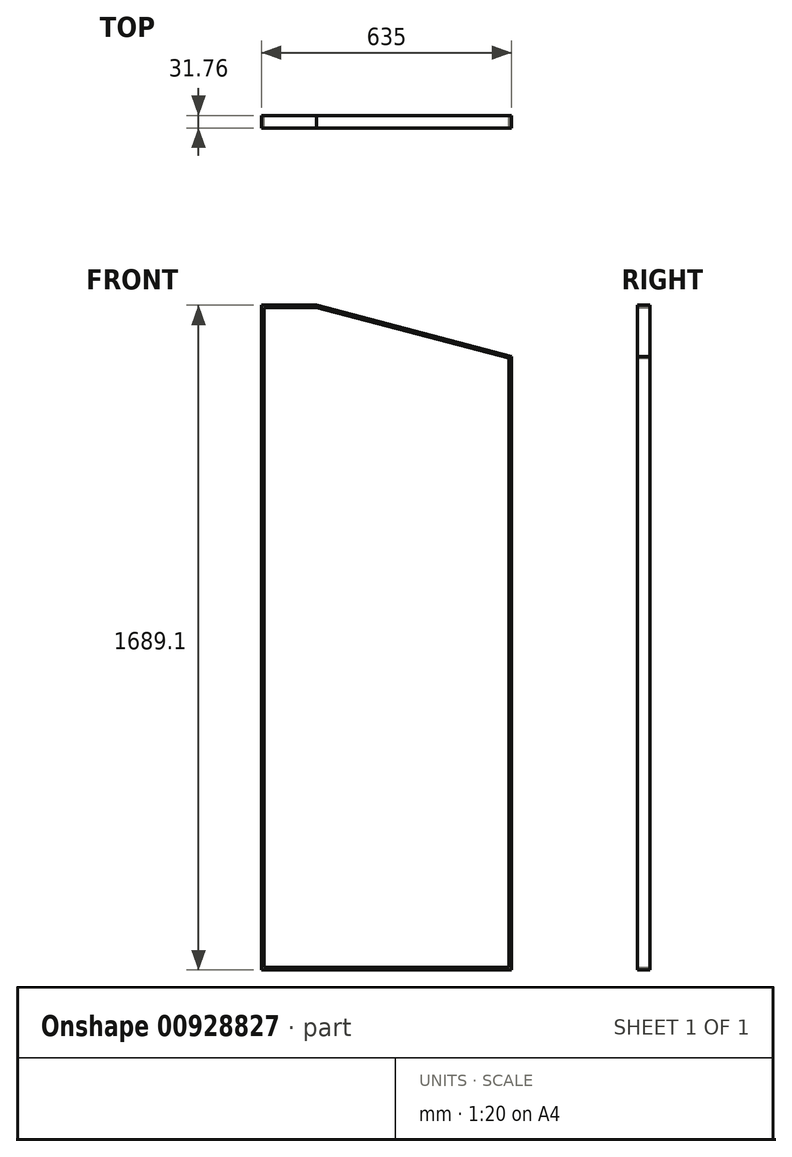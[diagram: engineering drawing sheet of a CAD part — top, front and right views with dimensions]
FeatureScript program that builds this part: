
annotation { "Feature Type Name" : "Feature", "Feature Type Description" : "" }
export const myFeature = defineFeature(function(context is Context, id is Id, definition is map)
    precondition{}
    {
        {
            var Q0;
            Q0=qCreatedBy(makeId("Front.planeOp"),FACE);
            var sketch = newSketch(context, id + "F0", { "sketchPlane" : qUnion([Q0])});
            skLineSegment(sketch, "E0.bottom", {"start": v(0, 0) * mm, "end": v(635, 0) * mm});
            skLineSegment(sketch, "E0.left", {"start": v(0, 0) * mm, "end": v(0, 1689.1) * mm});
            skLineSegment(sketch, "E0.right", {"start": v(635, 0) * mm, "end": v(635, 1558.93) * mm});
            skLineSegment(sketch, "E1", {"start": v(0, 1689.1) * mm, "end": v(139.7, 1689.1) * mm});
            skLineSegment(sketch, "E2", {"start": v(139.7, 1689.1) * mm, "end": v(635, 1558.92) * mm});
            skSolve(sketch);
        }
        {
            var Q0;
            Q0=makeQuery(id+"F0.imprint","IMPRINT",FACE,{"disambiguationData":[TD([[makeQuery(id+"F0.imprint","IMPRINT",EDGE,{"derivedFrom":sQuery(id+"F0.wireOp",EDGE,"E0.bottom")}),1.0]])]});
            extrude(context, id + "F1", {"entities" : qUnion([Q0]), "oppositeDirection" : true, "depth" : 1 / 101.6 * mm, "offsetDistance" : 25.4 * mm});
        }
        {
            var Q0;
            Q0=qCreatedBy(makeId("Front.planeOp"),FACE);
            var sketch = newSketch(context, id + "F2", { "sketchPlane" : qUnion([Q0])});
            skLineSegment(sketch, "E3.0.0", {"start": v(635, 1558.92) * mm, "end": v(139.7, 1689.1) * mm});
            skLineSegment(sketch, "E3.0.1", {"start": v(139.7, 1689.1) * mm, "end": v(0, 1689.1) * mm});
            skLineSegment(sketch, "E3.0.3", {"start": v(0, 0) * mm, "end": v(635, 0) * mm});
            skLineSegment(sketch, "E3.0.4", {"start": v(635, 0) * mm, "end": v(635, 1558.93) * mm});
            skLineSegment(sketch, "E4.bottom", {"start": v(0, 1689.1) * mm, "end": v(139.7, 1689.1) * mm});
            skLineSegment(sketch, "E4.top", {"start": v(6.35, 1682.75) * mm, "end": v(139.7, 1682.75) * mm});
            skLineSegment(sketch, "E5", {"start": v(139.7, 1689.1) * mm, "end": v(635, 1558.92) * mm});
            skLineSegment(sketch, "E6", {"start": v(139.7, 1682.75) * mm, "end": v(628.65, 1554.24) * mm});
            skLineSegment(sketch, "E7", {"start": v(0, 1689.1) * mm, "end": v(0, 0) * mm});
            skLineSegment(sketch, "E8", {"start": v(6.35, 1682.75) * mm, "end": v(6.35, 6.35) * mm});
            skPoint(sketch, "E9.orphan", {"position": v(0, 2.01) * mm});
            skLineSegment(sketch, "E10", {"start": v(6.35, 6.35) * mm, "end": v(628.65, 6.35) * mm});
            skLineSegment(sketch, "E11", {"start": v(628.65, 1554.24) * mm, "end": v(628.65, 6.35) * mm});
            skSolve(sketch);
        }
        {
            var Q0;
            Q0=makeQuery(id+"F2.imprint","IMPRINT",FACE,{"disambiguationData":[TD([[makeQuery(id+"F2.imprint","IMPRINT",EDGE,{"derivedFrom":sQuery(id+"F2.wireOp",EDGE,"E3.0.3")}),1.0]])]});
            extrude(context, id + "F3", {"entities" : qUnion([Q0]), "operationType" : NewBodyOperationType.ADD, "depth" : 31.75 * mm, "offsetDistance" : 25.4 * mm});
        }
    });
